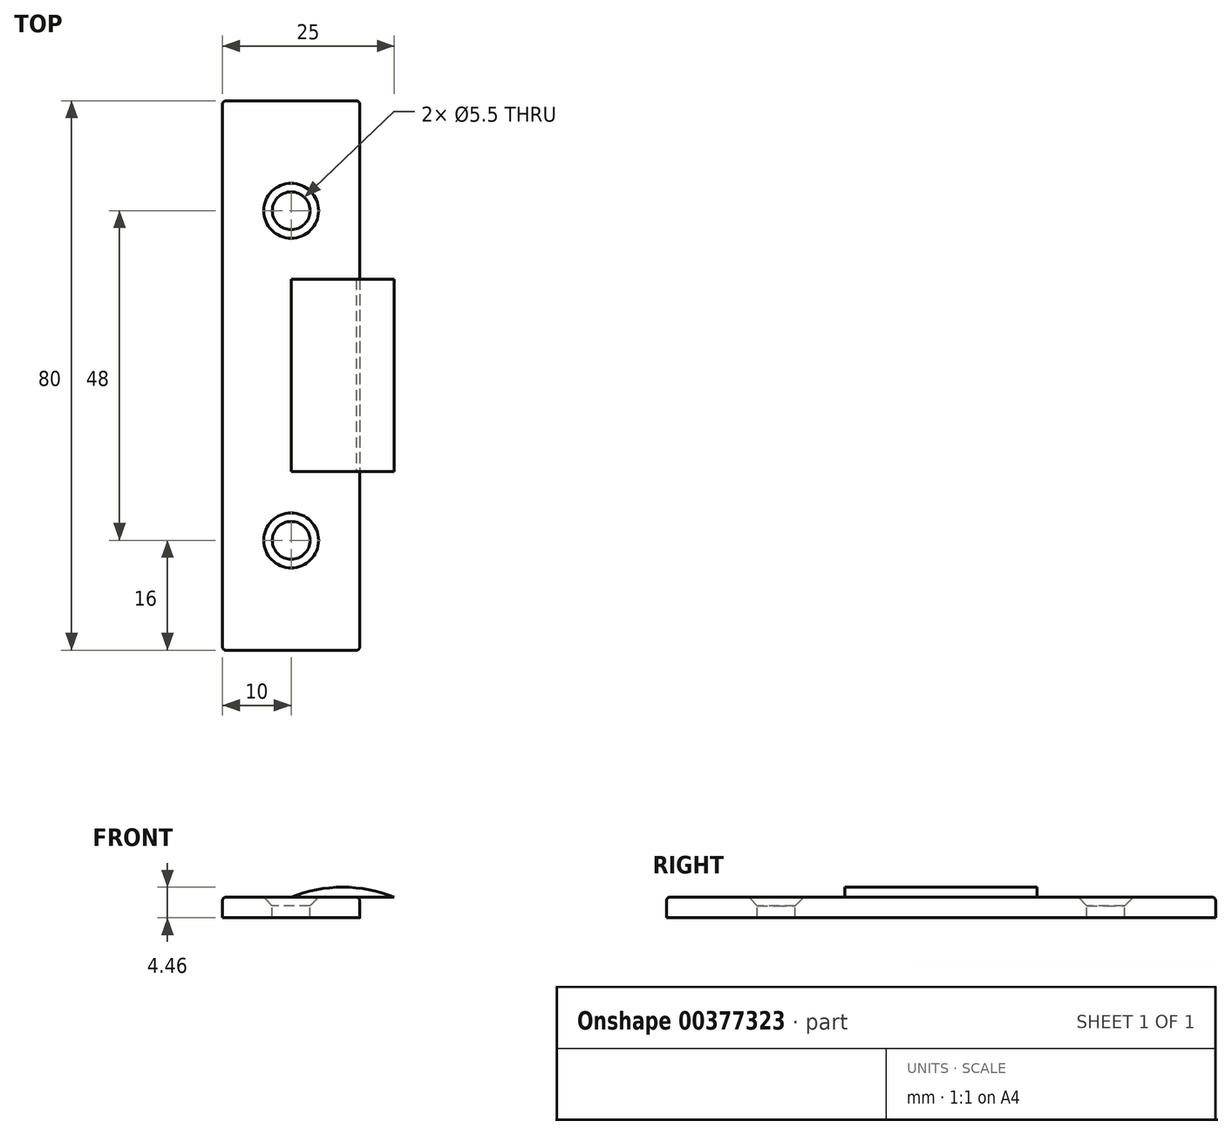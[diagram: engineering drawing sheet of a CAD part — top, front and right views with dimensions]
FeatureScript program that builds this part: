
annotation { "Feature Type Name" : "Feature", "Feature Type Description" : "" }
export const myFeature = defineFeature(function(context is Context, id is Id, definition is map)
    precondition{}
    {
        {
            var Q0;
            Q0=qCreatedBy(makeId("Top.planeOp"),FACE);
            var sketch = newSketch(context, id + "F0", { "sketchPlane" : qUnion([Q0])});
            skPoint(sketch, "E0", {"position": v(0, 0) * mm});
            skPoint(sketch, "E1", {"position": v(0, 48) * mm});
            skLineSegment(sketch, "E2.bottom", {"start": v(-10, 64) * mm, "end": v(10, 64) * mm});
            skLineSegment(sketch, "E2.top", {"start": v(-10, -16) * mm, "end": v(10, -16) * mm});
            skLineSegment(sketch, "E2.left", {"start": v(-10, 64) * mm, "end": v(-10, -16) * mm});
            skLineSegment(sketch, "E2.right", {"start": v(10, 64) * mm, "end": v(10, -16) * mm});
            skPoint(sketch, "E3", {"position": v(0, -16) * mm});
            skPoint(sketch, "E4", {"position": v(0, 64) * mm});
            skSolve(sketch);
        }
        {
            var Q0;
            Q0=makeQuery(id+"F0.imprint","IMPRINT",FACE,{"disambiguationData":[TD([[makeQuery(id+"F0.imprint","IMPRINT",EDGE,{"derivedFrom":sQuery(id+"F0.wireOp",EDGE,"E2.bottom")}),-1.0]])]});
            extrude(context, id + "F1", {"entities" : qUnion([Q0]), "depth" : 3 * mm});
        }
        {
            var Q0;
            Q0=qCreatedBy(makeId("Top.planeOp"),FACE);
            cPlane(context, id + "F2", {"entities" : qUnion([Q0]), "cplaneType" : CPlaneType.OFFSET, "offset" : 10.5 * mm, "width" : 150 * mm, "height" : 150 * mm});
        }
        {
            var Q0;
            Q0=makeQuery(id+"F1.opExtrude","SWEPT_FACE",FACE,{"disambiguationData":[OSD([sQuery(id+"F0.wireOp",EDGE,"E2.top")])]});
            var sketch = newSketch(context, id + "F3", { "sketchPlane" : qUnion([Q0])});
            skPoint(sketch, "E5", {"position": v(15, 3) * mm});
            skPoint(sketch, "E6", {"position": v(0, 3) * mm});
            skPoint(sketch, "E7", {"position": v(10, 3) * mm});
            skPoint(sketch, "E8", {"position": v(10, 0) * mm});
            skLineSegment(sketch, "E9", {"start": v(10, 0) * mm, "end": v(15, 0) * mm, "construction": true});
            skLineSegment(sketch, "E10", {"start": v(15, 0) * mm, "end": v(15, 3) * mm, "construction": true});
            skLineSegment(sketch, "E11", {"start": v(10, 3) * mm, "end": v(15, 3) * mm, "construction": true});
            skArc(sketch, "E12", {"start": v(15, 3) * mm, "mid": v(7.5, 4.46) * mm, "end": v(0, 3) * mm});
            skPoint(sketch, "E13", {"position": v(2, 3) * mm});
            skPoint(sketch, "E14", {"position": v(13, 3) * mm});
            skArc(sketch, "E15", {"start": v(13, 3) * mm, "mid": v(7.5, 3.86) * mm, "end": v(2, 3) * mm});
            skLineSegment(sketch, "E16", {"start": v(13, 3) * mm, "end": v(15, 3) * mm});
            skLineSegment(sketch, "E17", {"start": v(0, 3) * mm, "end": v(2, 3) * mm});
            skLineSegment(sketch, "E18", {"start": v(2, 3) * mm, "end": v(13, 3) * mm});
            skSolve(sketch);
        }
        {
            var Q0;
            Q0=makeQuery(id+"F1.opExtrude","CAP_FACE",FACE,{"disambiguationData":[OSD([sQuery(id+"F0.wireOp",EDGE,"E2.bottom"),sQuery(id+"F0.wireOp",EDGE,"E2.top"),sQuery(id+"F0.wireOp",EDGE,"E2.left"),sQuery(id+"F0.wireOp",EDGE,"E2.right")])],"isStart":false});
            var sketch = newSketch(context, id + "F4", { "sketchPlane" : qUnion([Q0])});
            skPoint(sketch, "E19", {"position": v(0, 48) * mm});
            skPoint(sketch, "E20", {"position": v(0, 0) * mm});
            skSolve(sketch);
        }
        {
            var Q0;
            Q0=sQuery(id+"F4.wireOp",VERTEX,"E20");
            var Q1;
            Q1=sQuery(id+"F4.wireOp",VERTEX,"E19");
            var Q2;
            Q2=makeQuery(id+"F1.opExtrude","SWEPT_BODY",BODY,{"disambiguationData":[OSD([sQuery(id+"F0.wireOp",EDGE,"E2.bottom"),sQuery(id+"F0.wireOp",EDGE,"E2.top"),sQuery(id+"F0.wireOp",EDGE,"E2.left"),sQuery(id+"F0.wireOp",EDGE,"E2.right")])]});
            hole(context, id + "F5", {"style" : HoleStyle.C_SINK, "endStyle" : HoleEndStyle.BLIND, "holeDiameter" : 5.5 * mm, "cSinkDiameter" : 8 * mm, "cSinkAngle" : 90 * degree, "holeDepth" : 15 * mm, "isTappedThrough" : true, "tappedDepth" : 12 * mm, "tapClearance" : 3, "locations" : qUnion([Q0, Q1]), "scope" : qUnion([Q2])});
        }
        {
            var Q0;
            Q0=qCreatedBy(makeId("Front.planeOp"),FACE);
            cPlane(context, id + "F6", {"entities" : qUnion([Q0]), "cplaneType" : CPlaneType.OFFSET, "offset" : 10 * mm, "oppositeDirection" : true, "width" : 150 * mm, "height" : 150 * mm});
        }
        {
            var Q0;
            Q0=makeQuery(id+"FH0GsJEzsSFQVmM_1.opExtrude","CAP_EDGE",EDGE,{"disambiguationData":[OSD([sQuery(id+"F1OQtBv7YCZJBjR_1.wireOp",EDGE,"969524ac-3ba3-4888-a7ee-3bf3de028013.0.4")])],"isStart":false});
            var Q1;
            Q1=makeQuery(id+"FH0GsJEzsSFQVmM_1.opExtrude","CAP_EDGE",EDGE,{"disambiguationData":[OSD([sQuery(id+"F1OQtBv7YCZJBjR_1.wireOp",EDGE,"969524ac-3ba3-4888-a7ee-3bf3de028013.0.4")])],"isStart":true});
            var Q2;
            Q2=makeQuery(id+"F1.opExtrude","CAP_EDGE",EDGE,{"disambiguationData":[OSD([sQuery(id+"F0.wireOp",EDGE,"E2.bottom")])],"isStart":false});
            var Q3;
            Q3=makeQuery(id+"F1.opExtrude","CAP_EDGE",EDGE,{"disambiguationData":[OSD([sQuery(id+"F0.wireOp",EDGE,"E2.left")])],"isStart":false});
            var Q4;
            {var subQ0=sQuery(id+"F0.wireOp",EDGE,"E2.bottom");var subQ1=sQuery(id+"F0.wireOp",EDGE,"E2.right");Q4=makeQuery(id+"FH0GsJEzsSFQVmM_1.boolean.opBoolean","SPLIT",EDGE,{"disambiguationData":[TD([makeQuery(id+"F1.opExtrude","SWEPT_FACE",FACE,{"disambiguationData":[OSD([subQ0])]})])],"derivedFrom":makeQuery(id+"F1.opExtrude","CAP_EDGE",EDGE,{"disambiguationData":[OSD([subQ1])],"isStart":false})});}
            var Q5;
            Q5=makeQuery(id+"F1.opExtrude","SWEPT_EDGE",EDGE,{"disambiguationData":[OSD([sQuery(id+"F0.wireOp",EDGE,"E2.top"),sQuery(id+"F0.wireOp",EDGE,"E2.left")])]});
            var Q6;
            Q6=makeQuery(id+"F1.opExtrude","SWEPT_EDGE",EDGE,{"disambiguationData":[OSD([sQuery(id+"F0.wireOp",EDGE,"E2.bottom"),sQuery(id+"F0.wireOp",EDGE,"E2.left")])]});
            fillet(context, id + "F7", {"entities" : qUnion([Q0, Q1, Q2, Q3, Q4, Q5, Q6]), "radius" : 0.5 * mm, "tangentPropagation" : true, "allowEdgeOverflow" : false});
        }
        {
            var Q0;
            Q0=makeQuery(id+"F1.opExtrude","SWEPT_EDGE",EDGE,{"disambiguationData":[OSD([sQuery(id+"F0.wireOp",EDGE,"E2.bottom"),sQuery(id+"F0.wireOp",EDGE,"E2.right")])]});
            var Q1;
            Q1=makeQuery(id+"F1.opExtrude","SWEPT_EDGE",EDGE,{"disambiguationData":[OSD([sQuery(id+"F0.wireOp",EDGE,"E2.top"),sQuery(id+"F0.wireOp",EDGE,"E2.right")])]});
            fillet(context, id + "F8", {"entities" : qUnion([Q0, Q1]), "radius" : 0.5 * mm, "tangentPropagation" : true, "allowEdgeOverflow" : false});
        }
        {
            var Q0;
            Q0=qCreatedBy(id+"F6.planeOp",FACE);
            var sketch = newSketch(context, id + "F9", { "sketchPlane" : qUnion([Q0])});
            skArc(sketch, "E21.0.0", {"start": v(2, 3) * mm, "mid": v(7.5, 3.86) * mm, "end": v(13, 3) * mm});
            skLineSegment(sketch, "E21.0.1", {"start": v(13, 3) * mm, "end": v(15, 3) * mm});
            skArc(sketch, "E21.0.2", {"start": v(15, 3) * mm, "mid": v(7.5, 4.46) * mm, "end": v(0, 3) * mm});
            skLineSegment(sketch, "E21.0.3", {"start": v(0, 3) * mm, "end": v(2, 3) * mm});
            skLineSegment(sketch, "E21.1.0", {"start": v(10, 3) * mm, "end": v(13, 3) * mm});
            skArc(sketch, "E21.1.1", {"start": v(13, 3) * mm, "mid": v(7.5, 3.86) * mm, "end": v(2, 3) * mm});
            skLineSegment(sketch, "E21.1.2", {"start": v(2, 3) * mm, "end": v(10, 3) * mm});
            skSolve(sketch);
        }
        {
            var Q0;
            Q0=makeQuery(id+"F9.imprint","IMPRINT",FACE,{"disambiguationData":[TD([[makeQuery(id+"F9.imprint","IMPRINT",EDGE,{"derivedFrom":sQuery(id+"F9.wireOp",EDGE,"E21.1.0")}),1.0]])]});
            var Q1;
            Q1=makeQuery(id+"F9.imprint","IMPRINT",FACE,{"disambiguationData":[TD([[makeQuery(id+"F9.imprint","IMPRINT",EDGE,{"derivedFrom":sQuery(id+"F9.wireOp",EDGE,"E21.0.1")}),1.0]])]});
            extrude(context, id + "F10", {"entities" : qUnion([Q0, Q1]), "operationType" : NewBodyOperationType.ADD, "oppositeDirection" : true, "depth" : 28 * mm});
        }
    });
